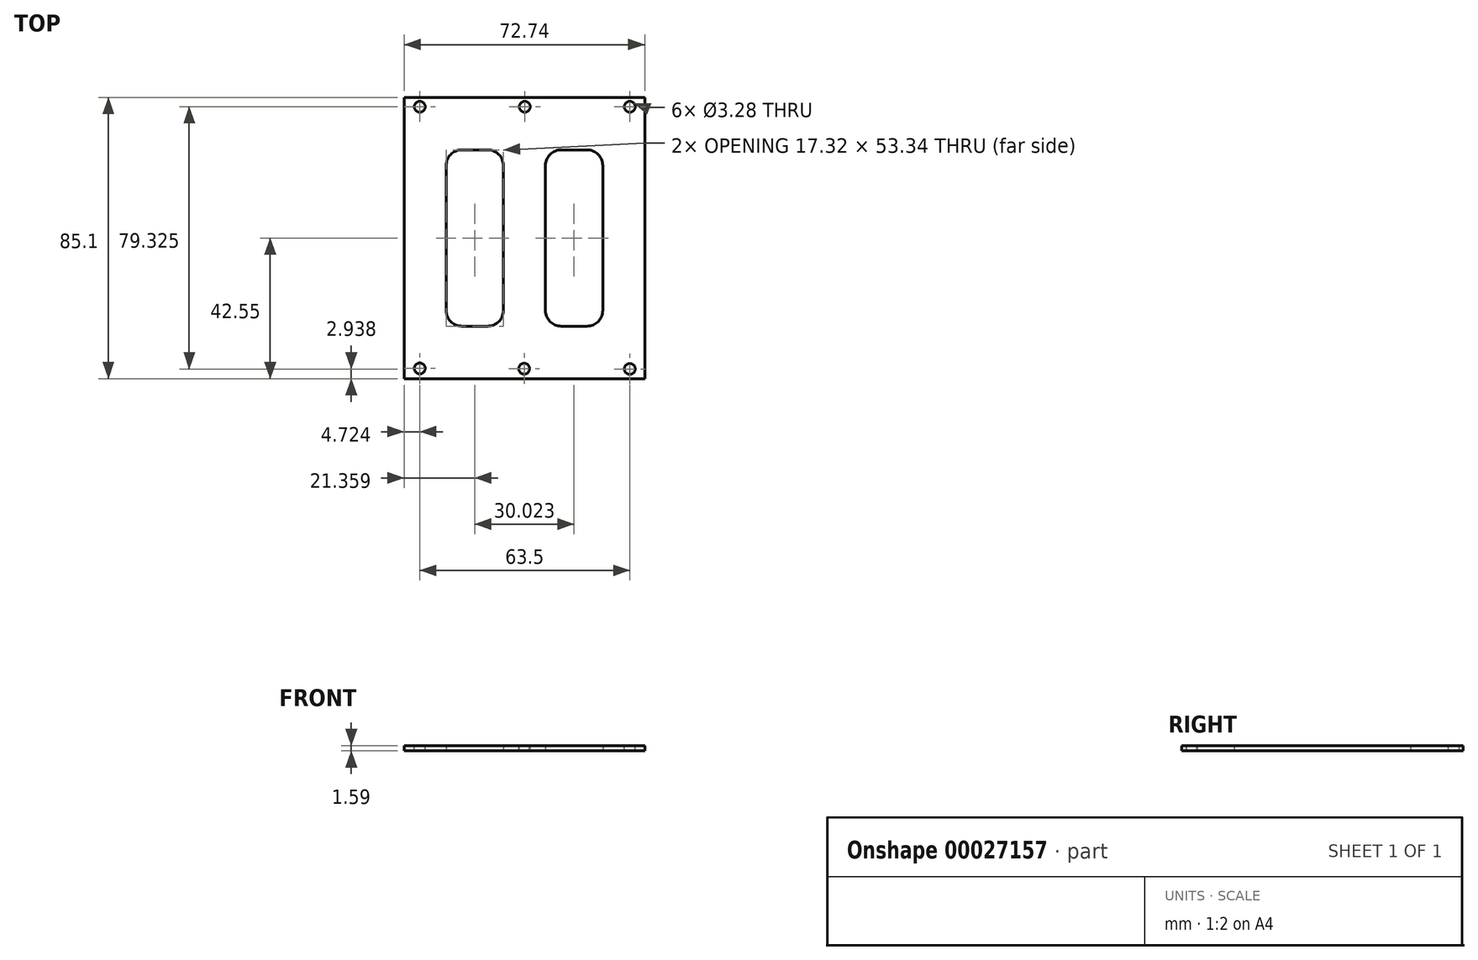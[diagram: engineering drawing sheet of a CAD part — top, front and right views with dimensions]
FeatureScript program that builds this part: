
annotation { "Feature Type Name" : "Feature", "Feature Type Description" : "" }
export const myFeature = defineFeature(function(context is Context, id is Id, definition is map)
    precondition{}
    {
        {
            var Q0;
            Q0=qCreatedBy(makeId("Top.planeOp"),FACE);
            var sketch = newSketch(context, id + "F0", { "sketchPlane" : qUnion([Q0])});
            skLineSegment(sketch, "E0.rect.bottom", {"start": v(36.37, 42.55) * mm, "end": v(-36.37, 42.55) * mm});
            skLineSegment(sketch, "E0.rect.top", {"start": v(36.37, -42.55) * mm, "end": v(-36.37, -42.55) * mm});
            skLineSegment(sketch, "E0.rect.left", {"start": v(36.37, 42.55) * mm, "end": v(36.37, -42.55) * mm});
            skLineSegment(sketch, "E0.rect.right", {"start": v(-36.37, 42.55) * mm, "end": v(-36.37, -42.55) * mm});
            skPoint(sketch, "E0.rect.middle", {"position": v(0, 0) * mm});
            skLineSegment(sketch, "E1.bottom", {"start": v(-18.9, 26.67) * mm, "end": v(-11.13, 26.67) * mm});
            skLineSegment(sketch, "E1.top", {"start": v(-18.9, -26.67) * mm, "end": v(-11.13, -26.67) * mm});
            skLineSegment(sketch, "E1.left", {"start": v(-23.67, 21.9) * mm, "end": v(-23.67, -21.9) * mm});
            skLineSegment(sketch, "E1.right", {"start": v(-6.35, 21.9) * mm, "end": v(-6.35, -21.9) * mm});
            skLineSegment(sketch, "E2.bottom", {"start": v(11.13, 26.67) * mm, "end": v(18.9, 26.67) * mm});
            skLineSegment(sketch, "E2.top", {"start": v(11.13, -26.67) * mm, "end": v(18.9, -26.67) * mm});
            skLineSegment(sketch, "E2.left", {"start": v(6.35, 21.9) * mm, "end": v(6.35, -21.9) * mm});
            skLineSegment(sketch, "E2.right", {"start": v(23.67, 21.9) * mm, "end": v(23.67, -21.9) * mm});
            skLineSegment(sketch, "E3", {"start": v(0, 0) * mm, "end": v(68.52, 0) * mm, "construction": true});
            skLineSegment(sketch, "E4", {"start": v(0, 0) * mm, "end": v(0, 50.3) * mm, "construction": true});
            skPoint(sketch, "E5.visualSharp", {"position": v(-23.67, 26.67) * mm});
            skArc(sketch, "E5.filletArc", {"start": v(-18.9, 26.67) * mm, "mid": v(-22.27, 25.27) * mm, "end": v(-23.67, 21.9) * mm});
            skPoint(sketch, "E6.visualSharp", {"position": v(-6.35, 26.67) * mm});
            skArc(sketch, "E6.filletArc", {"start": v(-6.35, 21.9) * mm, "mid": v(-7.75, 25.27) * mm, "end": v(-11.13, 26.67) * mm});
            skPoint(sketch, "E7.visualSharp", {"position": v(-6.35, -26.67) * mm});
            skArc(sketch, "E7.filletArc", {"start": v(-11.13, -26.67) * mm, "mid": v(-7.75, -25.27) * mm, "end": v(-6.35, -21.9) * mm});
            skPoint(sketch, "E8.visualSharp", {"position": v(-23.67, -26.67) * mm});
            skArc(sketch, "E8.filletArc", {"start": v(-23.67, -21.9) * mm, "mid": v(-22.27, -25.27) * mm, "end": v(-18.9, -26.67) * mm});
            skPoint(sketch, "E9.visualSharp", {"position": v(6.35, -26.67) * mm});
            skArc(sketch, "E9.filletArc", {"start": v(6.35, -21.9) * mm, "mid": v(7.75, -25.27) * mm, "end": v(11.13, -26.67) * mm});
            skPoint(sketch, "E10.visualSharp", {"position": v(23.67, -26.67) * mm});
            skArc(sketch, "E10.filletArc", {"start": v(18.9, -26.67) * mm, "mid": v(22.27, -25.27) * mm, "end": v(23.67, -21.9) * mm});
            skPoint(sketch, "E11.visualSharp", {"position": v(23.67, 26.67) * mm});
            skArc(sketch, "E11.filletArc", {"start": v(23.67, 21.9) * mm, "mid": v(22.27, 25.27) * mm, "end": v(18.9, 26.67) * mm});
            skPoint(sketch, "E12.visualSharp", {"position": v(6.35, 26.67) * mm});
            skArc(sketch, "E12.filletArc", {"start": v(11.13, 26.67) * mm, "mid": v(7.75, 25.27) * mm, "end": v(6.35, 21.9) * mm});
            skSolve(sketch);
        }
        {
            var Q0;
            Q0=makeQuery(id+"F0.imprint","IMPRINT",FACE,{"disambiguationData":[TD([[makeQuery(id+"F0.imprint","IMPRINT",EDGE,{"derivedFrom":sQuery(id+"F0.wireOp",EDGE,"E0.rect.bottom")}),1.0]])]});
            extrude(context, id + "F1", {"entities" : qUnion([Q0]), "depth" : 1.59 * mm});
        }
        {
            var Q0;
            Q0=makeQuery(id+"F1.opExtrude","CAP_FACE",FACE,{"disambiguationData":[OSD([sQuery(id+"F0.wireOp",EDGE,"E0.rect.bottom"),sQuery(id+"F0.wireOp",EDGE,"E0.rect.top"),sQuery(id+"F0.wireOp",EDGE,"E0.rect.left"),sQuery(id+"F0.wireOp",EDGE,"E0.rect.right"),sQuery(id+"F0.wireOp",EDGE,"E1.bottom"),sQuery(id+"F0.wireOp",EDGE,"E1.top"),sQuery(id+"F0.wireOp",EDGE,"E1.left"),sQuery(id+"F0.wireOp",EDGE,"E1.right"),sQuery(id+"F0.wireOp",EDGE,"E2.bottom"),sQuery(id+"F0.wireOp",EDGE,"E2.top"),sQuery(id+"F0.wireOp",EDGE,"E2.left"),sQuery(id+"F0.wireOp",EDGE,"E2.right"),sQuery(id+"F0.wireOp",EDGE,"E5.filletArc"),sQuery(id+"F0.wireOp",EDGE,"E6.filletArc"),sQuery(id+"F0.wireOp",EDGE,"E7.filletArc"),sQuery(id+"F0.wireOp",EDGE,"E8.filletArc"),sQuery(id+"F0.wireOp",EDGE,"E9.filletArc"),sQuery(id+"F0.wireOp",EDGE,"E10.filletArc"),sQuery(id+"F0.wireOp",EDGE,"E11.filletArc"),sQuery(id+"F0.wireOp",EDGE,"E12.filletArc")])],"isStart":false});
            var sketch = newSketch(context, id + "F2", { "sketchPlane" : qUnion([Q0])});
            skLineSegment(sketch, "E13", {"start": v(-31.65, 39.71) * mm, "end": v(31.85, 39.71) * mm});
            skLineSegment(sketch, "E14", {"start": v(31.85, 39.71) * mm, "end": v(31.85, -39.61) * mm});
            skLineSegment(sketch, "E15", {"start": v(-31.65, 39.71) * mm, "end": v(-31.65, -39.46) * mm});
            skLineSegment(sketch, "E16", {"start": v(-31.65, -39.46) * mm, "end": v(31.85, -39.61) * mm});
            skLineSegment(sketch, "E17", {"start": v(-0.09, -39.53) * mm, "end": v(0.1, 39.71) * mm});
            skCircle(sketch, "E18", {"center": v(-31.65, 39.71) * mm, "radius": 1.64 * mm});
            skCircle(sketch, "E19", {"center": v(0.1, 39.71) * mm, "radius": 1.64 * mm});
            skCircle(sketch, "E20", {"center": v(31.85, 39.71) * mm, "radius": 1.64 * mm});
            skCircle(sketch, "E21", {"center": v(-31.65, -39.46) * mm, "radius": 1.64 * mm});
            skCircle(sketch, "E22", {"center": v(-0.09, -39.53) * mm, "radius": 1.64 * mm});
            skCircle(sketch, "E23", {"center": v(31.85, -39.61) * mm, "radius": 1.64 * mm});
            skSolve(sketch);
        }
        {
            var Q0;
            Q0=sQuery(id+"F2.wireOp",VERTEX,"E15.start");
            var Q1;
            Q1=sQuery(id+"F2.wireOp",VERTEX,"E19.center");
            var Q2;
            Q2=sQuery(id+"F2.wireOp",VERTEX,"E14.start");
            var Q3;
            Q3=sQuery(id+"F2.wireOp",VERTEX,"E16.start");
            var Q4;
            Q4=sQuery(id+"F2.wireOp",VERTEX,"E22.center");
            var Q5;
            Q5=sQuery(id+"F2.wireOp",VERTEX,"E14.end");
            var Q6;
            Q6=makeQuery(id+"F1.opExtrude","SWEPT_BODY",BODY,{"disambiguationData":[OSD([sQuery(id+"F0.wireOp",EDGE,"E0.rect.bottom"),sQuery(id+"F0.wireOp",EDGE,"E0.rect.top"),sQuery(id+"F0.wireOp",EDGE,"E0.rect.left"),sQuery(id+"F0.wireOp",EDGE,"E0.rect.right"),sQuery(id+"F0.wireOp",EDGE,"E1.bottom"),sQuery(id+"F0.wireOp",EDGE,"E1.top"),sQuery(id+"F0.wireOp",EDGE,"E1.left"),sQuery(id+"F0.wireOp",EDGE,"E1.right"),sQuery(id+"F0.wireOp",EDGE,"E2.bottom"),sQuery(id+"F0.wireOp",EDGE,"E2.top"),sQuery(id+"F0.wireOp",EDGE,"E2.left"),sQuery(id+"F0.wireOp",EDGE,"E2.right"),sQuery(id+"F0.wireOp",EDGE,"E5.filletArc"),sQuery(id+"F0.wireOp",EDGE,"E6.filletArc"),sQuery(id+"F0.wireOp",EDGE,"E7.filletArc"),sQuery(id+"F0.wireOp",EDGE,"E8.filletArc"),sQuery(id+"F0.wireOp",EDGE,"E9.filletArc"),sQuery(id+"F0.wireOp",EDGE,"E10.filletArc"),sQuery(id+"F0.wireOp",EDGE,"E11.filletArc"),sQuery(id+"F0.wireOp",EDGE,"E12.filletArc")])]});
            hole(context, id + "F3", {"style" : HoleStyle.SIMPLE, "holeDiameter" : 3.28 * mm, "endStyle" : HoleEndStyle.THROUGH, "locations" : qUnion([Q0, Q1, Q2, Q3, Q4, Q5]), "scope" : qUnion([Q6])});
        }
    });
